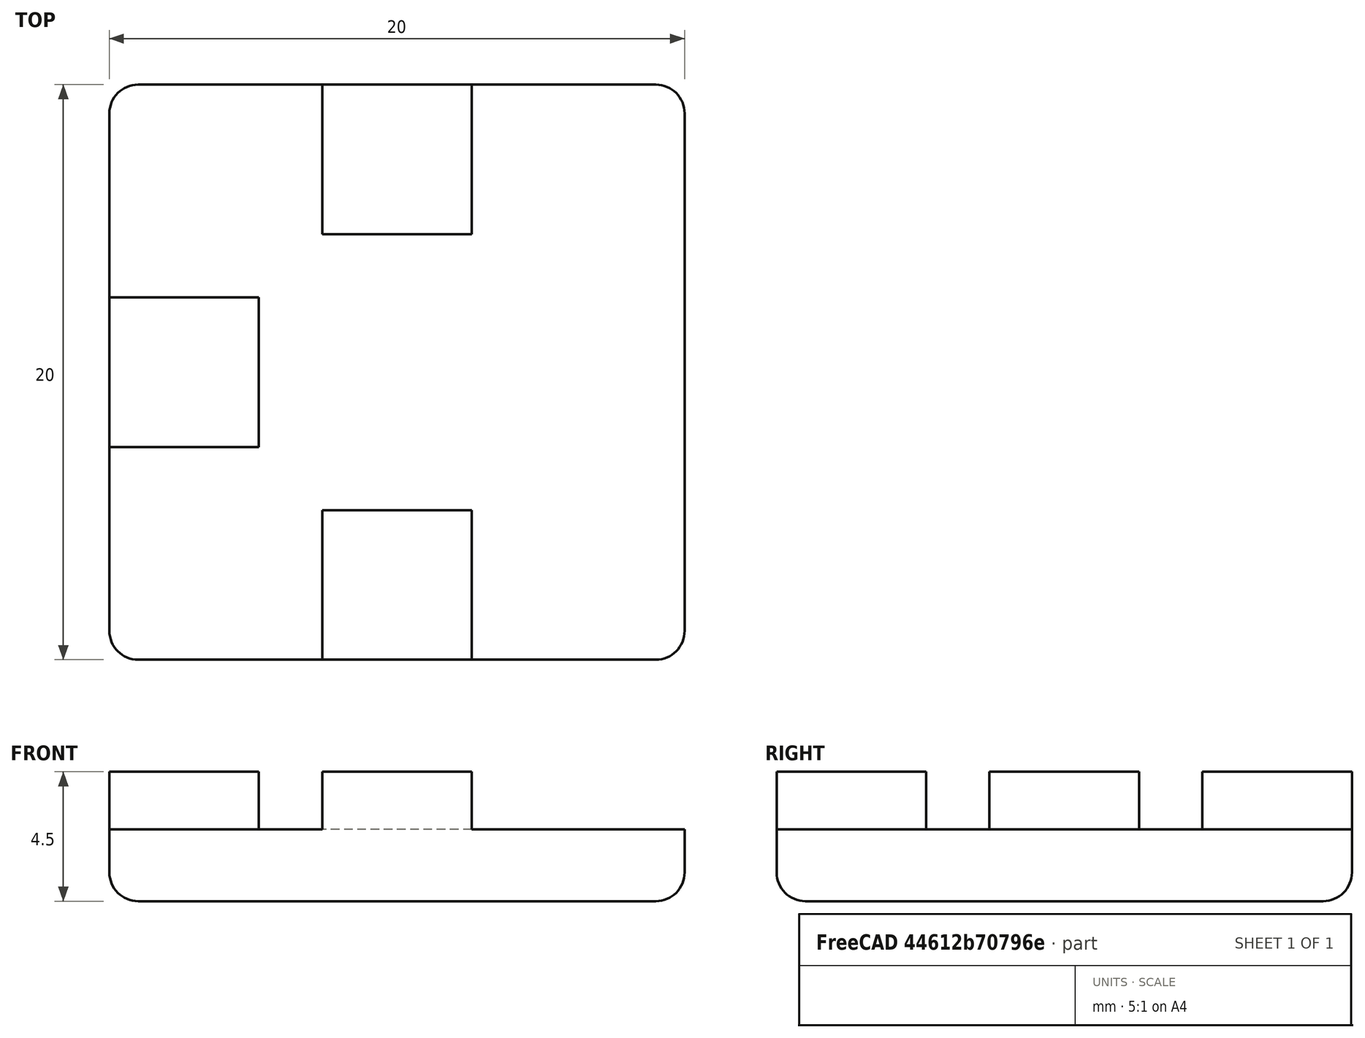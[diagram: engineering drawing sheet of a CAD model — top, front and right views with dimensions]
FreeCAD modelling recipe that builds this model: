
FCSTD DOCUMENT  (FreeCAD 0.16R6707 (Git))
Label: my2020endcap
License: All rights reserved
LicenseURL: http://en.wikipedia.org/wiki/All_rights_reserved
objects: Part::Box×4, Part::Fillet×2, Part::MultiFuse×1
note: 7 computed .brp shape members not serialized (recipe doc carries the construction recipe); baked Part::Feature solids carry a one-line shape summary decoded from their .brp

FEATURE [Part::Box] Box  label="Würfel"
  Height = 2.5
  Length = 20
  Width = 20
FEATURE [Part::Fillet] Fillet
  Base = -> Box
  Edges = 4 edges r=1: [Edge1,Edge3,Edge5,Edge7]
FEATURE [Part::Fillet] Fillet001
  Base = -> Fillet
  Edges = 8 edges r=1: [Edge4,Edge12,Edge14,Edge16,Edge17,Edge18,Edge19,Edge20]
FEATURE [Part::Box] Box001  label="Würfel001"
  Height = 3
  Length = 5.2
  Placement = pos=(7.4,0,1.5) rot=(0,0,1;0rad)
  Width = 5.2
FEATURE [Part::Box] Box002  label="Würfel002"
  Height = 3
  Length = 5.2
  Placement = pos=(7.4,14.8,1.5) rot=(0,0,1;0rad)
  Width = 5.2
FEATURE [Part::Box] Box003  label="Würfel003"
  Height = 3
  Length = 5.2
  Placement = pos=(0,7.4,1.5) rot=(0,0,1;0rad)
  Width = 5.2
FEATURE [Part::MultiFuse] Fusion
  Shapes = -> [Fillet001,Box001,Box003,Box002]
